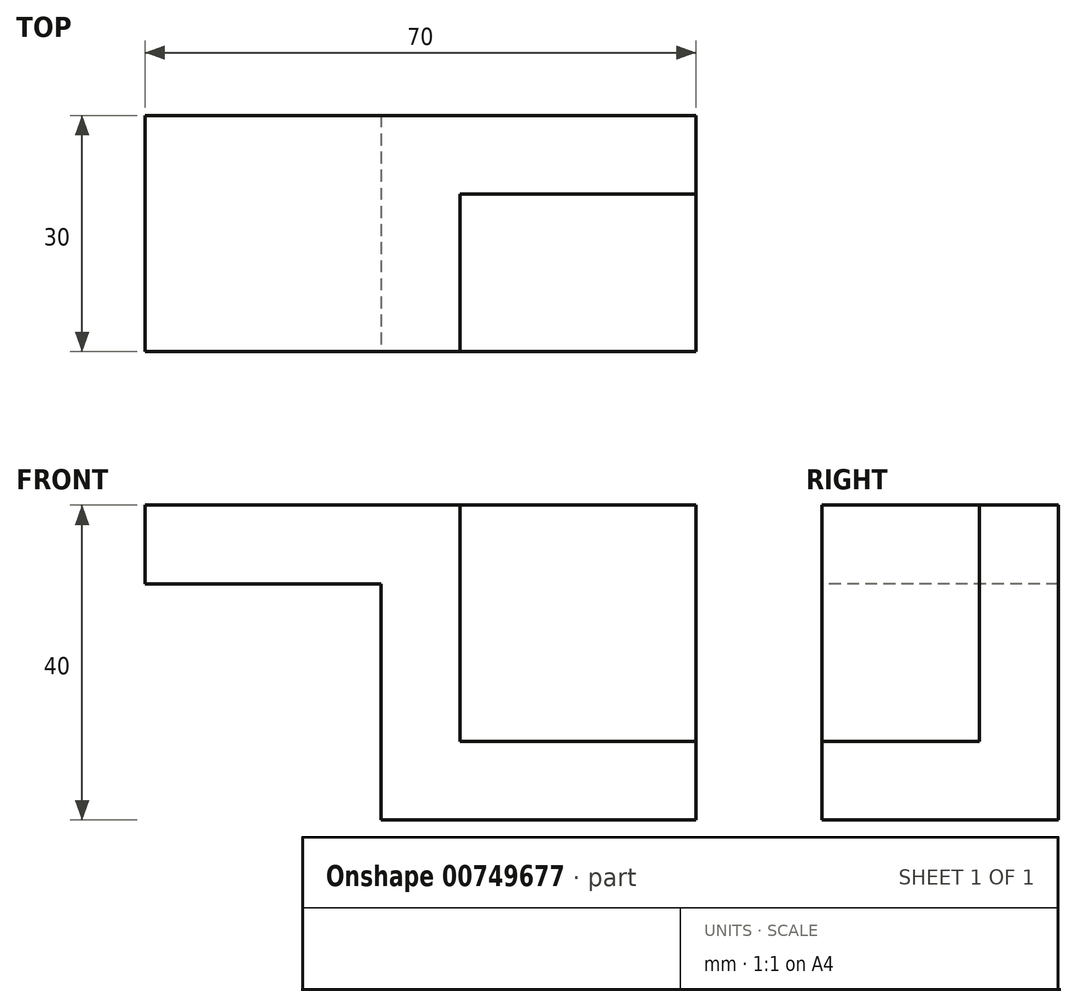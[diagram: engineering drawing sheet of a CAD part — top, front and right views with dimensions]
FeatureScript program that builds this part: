
annotation { "Feature Type Name" : "Feature", "Feature Type Description" : "" }
export const myFeature = defineFeature(function(context is Context, id is Id, definition is map)
    precondition{}
    {
        {
            var Q0;
            Q0=qCreatedBy(makeId("Front.planeOp"),FACE);
            var sketch = newSketch(context, id + "F0", { "sketchPlane" : qUnion([Q0])});
            skLineSegment(sketch, "E0.bottom", {"start": v(-70, 40) * mm, "end": v(0, 40) * mm});
            skLineSegment(sketch, "E0.top", {"start": v(-70, 0) * mm, "end": v(0, 0) * mm});
            skLineSegment(sketch, "E0.left", {"start": v(-70, 40) * mm, "end": v(-70, 0) * mm});
            skLineSegment(sketch, "E0.right", {"start": v(0, 40) * mm, "end": v(0, 0) * mm});
            skLineSegment(sketch, "E1", {"start": v(-70, 30) * mm, "end": v(-40, 30) * mm});
            skLineSegment(sketch, "E2", {"start": v(-40, 30) * mm, "end": v(-40, 0) * mm});
            skLineSegment(sketch, "E3", {"start": v(-30, 40) * mm, "end": v(-30, 10) * mm});
            skLineSegment(sketch, "E4", {"start": v(-30, 10) * mm, "end": v(0, 10) * mm});
            skSolve(sketch);
        }
        {
            var Q0;
            {var subQ7=sQuery(id+"F0.wireOp",EDGE,"E1");Q0=makeQuery(id+"F0.imprint","IMPRINT",FACE,{"disambiguationData":[TD([[makeQuery(id+"F0.imprint","IMPRINT",EDGE,{"derivedFrom":subQ7}),1.0]])]});}
            var Q1;
            {var subQ3=sQuery(id+"F0.wireOp",EDGE,"E3");Q1=makeQuery(id+"F0.imprint","IMPRINT",FACE,{"disambiguationData":[TD([[makeQuery(id+"F0.imprint","IMPRINT",EDGE,{"derivedFrom":subQ3}),1.0]])]});}
            extrude(context, id + "F1", {"entities" : qUnion([Q0, Q1]), "oppositeDirection" : true, "depth" : 30 * mm, "offsetDistance" : 25 * mm});
        }
        {
            var Q0;
            {var subQ3=sQuery(id+"F0.wireOp",EDGE,"E3");Q0=makeQuery(id+"F0.imprint","IMPRINT",FACE,{"disambiguationData":[TD([[makeQuery(id+"F0.imprint","IMPRINT",EDGE,{"derivedFrom":subQ3}),1.0]])]});}
            extrude(context, id + "F2", {"entities" : qUnion([Q0]), "operationType" : NewBodyOperationType.REMOVE, "oppositeDirection" : true, "depth" : 20 * mm, "offsetDistance" : 25 * mm});
        }
    });
